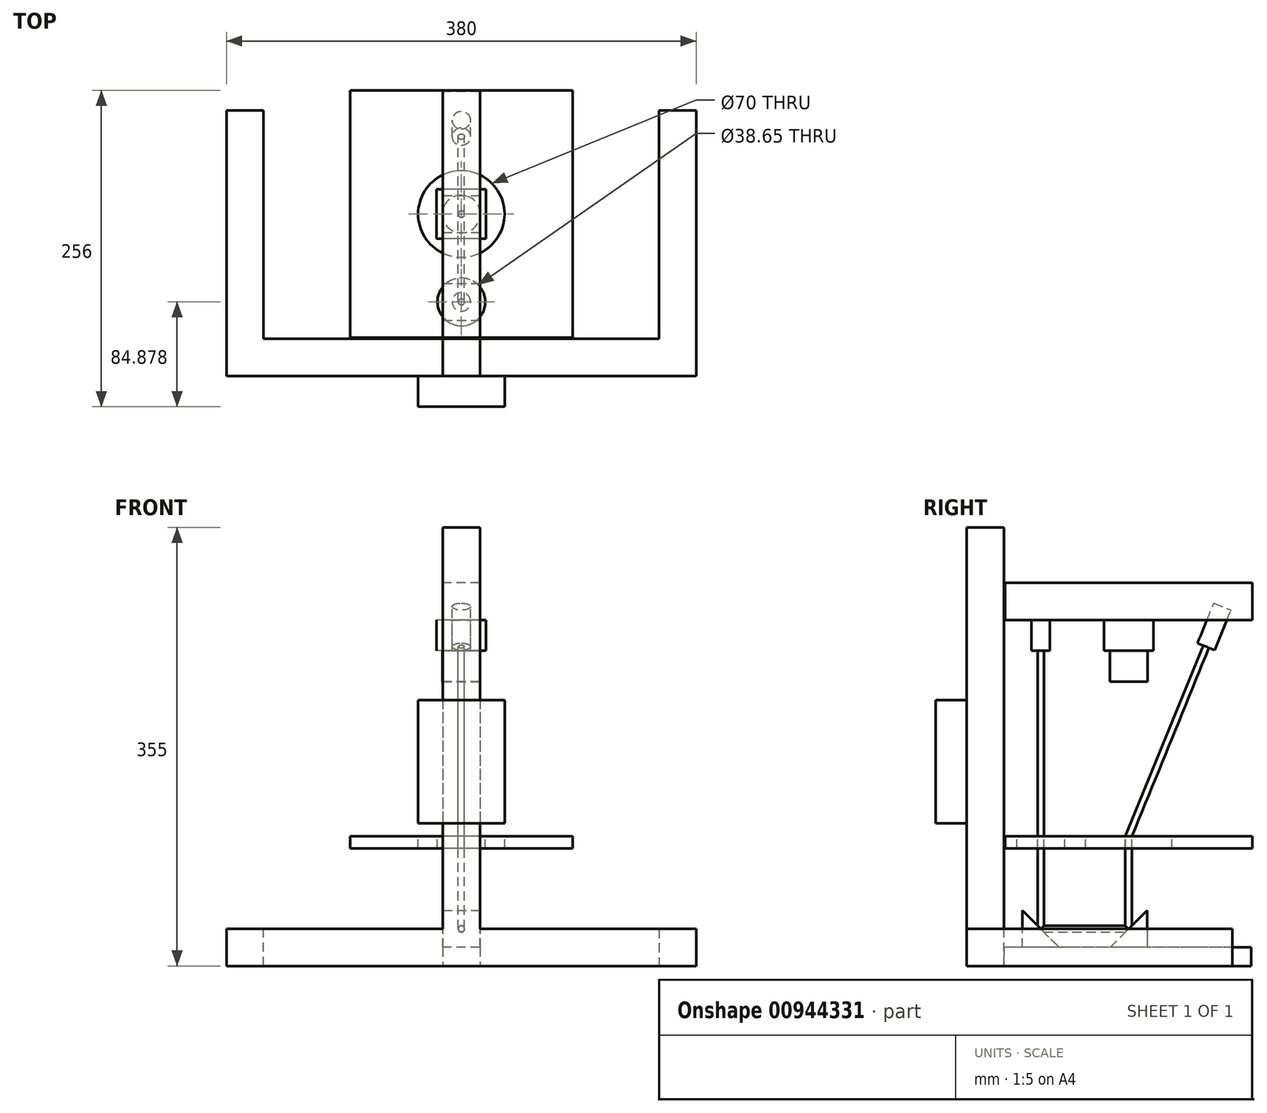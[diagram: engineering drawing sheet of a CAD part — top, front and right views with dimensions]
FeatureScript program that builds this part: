
annotation { "Feature Type Name" : "Feature", "Feature Type Description" : "" }
export const myFeature = defineFeature(function(context is Context, id is Id, definition is map)
    precondition{}
    {
        {
            assignVariable(context, id + "F0", {"name" : "Seccion", "anyValue" : 30});
        }
        {
            assignVariable(context, id + "F1", {"name" : "AxisX", "anyValue" : 200});
        }
        {
            assignVariable(context, id + "F2", {"name" : "AxisY", "anyValue" : 350});
        }
        {
            assignVariable(context, id + "F3", {"name" : "AxisZ", "anyValue" : 340});
        }
        {
            var Q0;
            Q0=qCreatedBy(makeId("Top.planeOp"),FACE);
            var sketch = newSketch(context, id + "F4", { "sketchPlane" : qUnion([Q0])});
            skLineSegment(sketch, "E0", {"start": v(-141.57, 101.23) * mm, "end": v(-141.57, -98.77) * mm});
            skLineSegment(sketch, "E1", {"start": v(-141.57, -98.77) * mm, "end": v(208.43, -98.77) * mm});
            skLineSegment(sketch, "E2", {"start": v(208.43, -98.77) * mm, "end": v(208.43, 101.23) * mm});
            skPoint(sketch, "E3", {"position": v(33.43, -98.77) * mm});
            skLineSegment(sketch, "E4.bottom", {"start": v(18.43, -83.77) * mm, "end": v(48.43, -83.77) * mm});
            skLineSegment(sketch, "E4.top", {"start": v(18.43, -113.77) * mm, "end": v(48.43, -113.77) * mm});
            skLineSegment(sketch, "E4.left", {"start": v(18.43, -83.77) * mm, "end": v(18.43, -113.77) * mm});
            skLineSegment(sketch, "E4.right", {"start": v(48.43, -83.77) * mm, "end": v(48.43, -113.77) * mm});
            skSolve(sketch);
        }
        {
            var Q0;
            {var subQ5=sQuery(id+"F4.wireOp",EDGE,"E4.bottom");Q0=makeQuery(id+"F4.imprint","IMPRINT",FACE,{"disambiguationData":[TD([[makeQuery(id+"F4.imprint","IMPRINT",EDGE,{"derivedFrom":subQ5}),-1.0]])]});}
            var Q1;
            {var subQ5=sQuery(id+"F4.wireOp",EDGE,"E4.top");Q1=makeQuery(id+"F4.imprint","IMPRINT",FACE,{"disambiguationData":[TD([[makeQuery(id+"F4.imprint","IMPRINT",EDGE,{"derivedFrom":subQ5}),1.0]])]});}
            extrude(context, id + "F5", {"entities" : qUnion([Q0, Q1]), "depth" : (getVariable(context, 'AxisZ')) * mm, "offsetDistance" : 25 * mm});
        }
        {
            var Q0;
            Q0=qCreatedBy(makeId("Front.planeOp"),FACE);
            var Q1;
            Q1=sQuery(id+"F4.wireOp",VERTEX,"E0.start");
            cPlane(context, id + "F6", {"entities" : qUnion([Q0, Q1]), "cplaneType" : CPlaneType.PLANE_POINT, "offset" : 25 * mm, "width" : 150 * mm, "height" : 150 * mm});
        }
        {
            var Q0;
            Q0=qCreatedBy(id+"F6.planeOp",FACE);
            var sketch = newSketch(context, id + "F7", { "sketchPlane" : qUnion([Q0])});
            skLineSegment(sketch, "E5.bottom", {"start": v(-126.57, 15) * mm, "end": v(-156.57, 15) * mm});
            skLineSegment(sketch, "E5.top", {"start": v(-126.57, -15) * mm, "end": v(-156.57, -15) * mm});
            skLineSegment(sketch, "E5.left", {"start": v(-126.57, 15) * mm, "end": v(-126.57, -15) * mm});
            skLineSegment(sketch, "E5.right", {"start": v(-156.57, 15) * mm, "end": v(-156.57, -15) * mm});
            skPoint(sketch, "E5.middle", {"position": v(-141.57, 0) * mm});
            skLineSegment(sketch, "E6.bottom", {"start": v(223.43, 15) * mm, "end": v(193.43, 15) * mm});
            skLineSegment(sketch, "E6.top", {"start": v(223.43, -15) * mm, "end": v(193.43, -15) * mm});
            skLineSegment(sketch, "E6.left", {"start": v(223.43, 15) * mm, "end": v(223.43, -15) * mm});
            skLineSegment(sketch, "E6.right", {"start": v(193.43, 15) * mm, "end": v(193.43, -15) * mm});
            skPoint(sketch, "E6.middle", {"position": v(208.43, 0) * mm});
            skSolve(sketch);
        }
        {
            var Q0;
            Q0=makeQuery(id+"F7.imprint","IMPRINT",FACE,{"disambiguationData":[TD([[makeQuery(id+"F7.imprint","IMPRINT",EDGE,{"derivedFrom":sQuery(id+"F7.wireOp",EDGE,"E6.bottom")}),1.0]])]});
            var Q1;
            Q1=makeQuery(id+"F7.imprint","IMPRINT",FACE,{"disambiguationData":[TD([[makeQuery(id+"F7.imprint","IMPRINT",EDGE,{"derivedFrom":sQuery(id+"F7.wireOp",EDGE,"E5.bottom")}),1.0]])]});
            extrude(context, id + "F8", {"entities" : qUnion([Q0, Q1]), "depth" : (getVariable(context, 'AxisX') + getVariable(context, 'Seccion') / 2) * mm, "offsetDistance" : 25 * mm});
        }
        {
            var Q0;
            Q0=makeQuery(id+"F8.opExtrude","SWEPT_FACE",FACE,{"disambiguationData":[OSD([sQuery(id+"F7.wireOp",EDGE,"E5.right")])]});
            var sketch = newSketch(context, id + "F9", { "sketchPlane" : qUnion([Q0])});
            skLineSegment(sketch, "E7.bottom", {"start": v(113.77, 15) * mm, "end": v(83.77, 15) * mm});
            skLineSegment(sketch, "E7.top", {"start": v(113.77, -15) * mm, "end": v(83.77, -15) * mm});
            skLineSegment(sketch, "E7.left", {"start": v(113.77, 15) * mm, "end": v(113.77, -15) * mm});
            skLineSegment(sketch, "E7.right", {"start": v(83.77, 15) * mm, "end": v(83.77, -15) * mm});
            skSolve(sketch);
        }
        {
            var Q0;
            {var subQ4=sQuery(id+"F12.wireOp",EDGE,"E8.top");Q0=makeQuery(id+"F12.imprint","IMPRINT",FACE,{"disambiguationData":[TD([[makeQuery(id+"F12.imprint","IMPRINT",EDGE,{"derivedFrom":subQ4}),-1.0]])]});}
            var Q1;
            Q1=makeQuery(id+"F5.opExtrude","SWEPT_FACE",FACE,{"disambiguationData":[OSD([sQuery(id+"F4.wireOp",EDGE,"E4.bottom")])]});
            cPlane(context, id + "F10", {"entities" : qUnion([Q0, Q1]), "cplaneType" : CPlaneType.OFFSET, "offset" : 1 * mm, "width" : 150 * mm, "height" : 150 * mm});
        }
        {
            var Q0;
            Q0=makeQuery(id+"F9.imprint","IMPRINT",FACE,{"disambiguationData":[TD([[makeQuery(id+"F9.imprint","IMPRINT",EDGE,{"derivedFrom":sQuery(id+"F9.wireOp",EDGE,"E7.bottom")}),1.0]])]});
            extrude(context, id + "F11", {"entities" : qUnion([Q0]), "operationType" : NewBodyOperationType.ADD, "oppositeDirection" : true, "depth" : (getVariable(context, 'AxisY')) * mm, "offsetDistance" : 25 * mm});
        }
        {
            var Q0;
            Q0=qCreatedBy(id+"F10.planeOp",FACE);
            var sketch = newSketch(context, id + "F12", { "sketchPlane" : qUnion([Q0])});
            skLineSegment(sketch, "E8.bottom", {"start": v(-48.43, 295) * mm, "end": v(-18.43, 295) * mm});
            skLineSegment(sketch, "E8.top", {"start": v(-48.43, 265) * mm, "end": v(-18.43, 265) * mm});
            skLineSegment(sketch, "E8.left", {"start": v(-48.43, 295) * mm, "end": v(-48.43, 265) * mm});
            skLineSegment(sketch, "E8.right", {"start": v(-18.43, 295) * mm, "end": v(-18.43, 265) * mm});
            skLineSegment(sketch, "E9", {"start": v(-33.43, 265) * mm, "end": v(-33.43, -15) * mm, "construction": true});
            skLineSegment(sketch, "E10.bottom", {"start": v(-123.43, 90) * mm, "end": v(56.57, 90) * mm});
            skLineSegment(sketch, "E10.top", {"start": v(-123.43, 80) * mm, "end": v(56.57, 80) * mm});
            skLineSegment(sketch, "E10.left", {"start": v(-123.43, 90) * mm, "end": v(-123.43, 80) * mm});
            skLineSegment(sketch, "E10.right", {"start": v(56.57, 90) * mm, "end": v(56.57, 80) * mm});
            skPoint(sketch, "E10.middle", {"position": v(-33.43, 85) * mm});
            skLineSegment(sketch, "E11", {"start": v(-123.43, 80) * mm, "end": v(-123.43, 0) * mm, "construction": true});
            skSolve(sketch);
        }
        {
            var Q0;
            Q0=makeQuery(id+"F12.imprint","IMPRINT",FACE,{"disambiguationData":[TD([[makeQuery(id+"F12.imprint","IMPRINT",EDGE,{"derivedFrom":sQuery(id+"F12.wireOp",EDGE,"E8.bottom")}),-1.0]])]});
            extrude(context, id + "F13", {"entities" : qUnion([Q0]), "operationType" : NewBodyOperationType.ADD, "depth" : (getVariable(context, 'AxisX')) * mm, "offsetDistance" : 25 * mm});
        }
        {
            var Q0;
            Q0=makeQuery(id+"F12.imprint","IMPRINT",FACE,{"disambiguationData":[TD([[makeQuery(id+"F12.imprint","IMPRINT",EDGE,{"derivedFrom":sQuery(id+"F12.wireOp",EDGE,"E10.bottom")}),-1.0]])]});
            extrude(context, id + "F14", {"entities" : qUnion([Q0]), "depth" : (getVariable(context, 'AxisX')) * mm, "offsetDistance" : 25 * mm});
        }
        {
            var Q0;
            Q0=makeQuery(id+"F14.opExtrude","SWEPT_FACE",FACE,{"disambiguationData":[OSD([sQuery(id+"F12.wireOp",EDGE,"E10.bottom")])]});
            var sketch = newSketch(context, id + "F15", { "sketchPlane" : qUnion([Q0])});
            skCircle(sketch, "E12", {"center": v(33.43, 17.23) * mm, "radius": 35 * mm});
            skPoint(sketch, "E12.centerSnap0", {"position": v(123.43, 17.23) * mm});
            skPoint(sketch, "E12.centerSnap1", {"position": v(33.43, -82.77) * mm});
            skLineSegment(sketch, "E13", {"start": v(33.43, -82.77) * mm, "end": v(33.43, 17.23) * mm, "construction": true});
            skCircle(sketch, "E14", {"center": v(33.43, -53.9) * mm, "radius": 19.32 * mm});
            skCircle(sketch, "E15", {"center": v(33.43, 17.23) * mm, "radius": 2.5 * mm});
            skSolve(sketch);
        }
        {
            var Q0;
            Q0=makeQuery(id+"F15.imprint","IMPRINT",FACE,{"disambiguationData":[TD([[makeQuery(id+"F15.imprint","IMPRINT",EDGE,{"derivedFrom":sQuery(id+"F15.wireOp",EDGE,"E14")}),1.0]])]});
            var Q1;
            Q1=makeQuery(id+"F15.imprint","IMPRINT",FACE,{"disambiguationData":[TD([[makeQuery(id+"F15.imprint","IMPRINT",EDGE,{"derivedFrom":sQuery(id+"F15.wireOp",EDGE,"E12")}),1.0]])]});
            var Q2;
            Q2=makeQuery(id+"F15.imprint","IMPRINT",FACE,{"disambiguationData":[TD([[makeQuery(id+"F15.imprint","IMPRINT",EDGE,{"derivedFrom":sQuery(id+"F15.wireOp",EDGE,"E15")}),1.0]])]});
            extrude(context, id + "F16", {"entities" : qUnion([Q0, Q1, Q2]), "operationType" : NewBodyOperationType.REMOVE, "oppositeDirection" : true, "depth" : 10 * mm, "offsetDistance" : 25 * mm});
        }
        {
            var Q0;
            Q0=makeQuery(id+"F13.opExtrude","SWEPT_FACE",FACE,{"disambiguationData":[OSD([sQuery(id+"F12.wireOp",EDGE,"E8.top")])]});
            var sketch = newSketch(context, id + "F17", { "sketchPlane" : qUnion([Q0])});
            skPoint(sketch, "E16.middle", {"position": v(33.43, -17.23) * mm});
            skPoint(sketch, "E16.middle.positionSnap0", {"position": v(48.43, -17.23) * mm});
            skPoint(sketch, "E16.centerSnap0", {"position": v(48.43, -17.23) * mm});
            skLineSegment(sketch, "E17.bottom", {"start": v(53.43, 2.77) * mm, "end": v(13.43, 2.77) * mm});
            skLineSegment(sketch, "E17.top", {"start": v(53.43, -37.23) * mm, "end": v(13.43, -37.23) * mm});
            skLineSegment(sketch, "E17.left", {"start": v(53.43, 2.77) * mm, "end": v(53.43, -37.23) * mm});
            skLineSegment(sketch, "E17.right", {"start": v(13.43, 2.77) * mm, "end": v(13.43, -37.23) * mm});
            skSolve(sketch);
        }
        {
            var Q0;
            {var subQ0=sQuery(id+"F17.wireOp",EDGE,"E17.bottom");var subQ1=sQuery(id+"F12.wireOp",EDGE,"E8.top");var subQ2=makeQuery(id+"F13.opExtrude","SWEPT_EDGE",EDGE,{"disambiguationData":[OSD([subQ1,sQuery(id+"F12.wireOp",EDGE,"E8.left")])]});var subQ3=makeQuery(id+"F17.imprint","INTERSECT",VERTEX,{"derivedFrom":[subQ2,subQ0]});Q0=makeQuery(id+"F17.imprint","IMPRINT",FACE,{"disambiguationData":[TD([[makeQuery(id+"F17.imprint","IMPRINT",EDGE,{"disambiguationData":[TD([[subQ3,-1.0]])],"derivedFrom":subQ0}),1.0]])]});}
            var Q1;
            {var subQ4=sQuery(id+"F17.wireOp",EDGE,"E17.right");Q1=makeQuery(id+"F17.imprint","IMPRINT",FACE,{"disambiguationData":[TD([[makeQuery(id+"F17.imprint","IMPRINT",EDGE,{"derivedFrom":subQ4}),1.0]])]});}
            var Q2;
            {var subQ4=sQuery(id+"F17.wireOp",EDGE,"E17.left");Q2=makeQuery(id+"F17.imprint","IMPRINT",FACE,{"disambiguationData":[TD([[makeQuery(id+"F17.imprint","IMPRINT",EDGE,{"derivedFrom":subQ4}),-1.0]])]});}
            var Q3;
            {var subQ0=sQuery(id+"F17.wireOp",EDGE,"qo7p0JnK-KsdK-9qBr-5w5p-VYG7PEEHzOIh");var subQ1=sQuery(id+"F12.wireOp",EDGE,"E8.top");var subQ2=makeQuery(id+"F13.opExtrude","SWEPT_EDGE",EDGE,{"disambiguationData":[OSD([subQ1,sQuery(id+"F12.wireOp",EDGE,"E8.right")])]});var subQ3=makeQuery(id+"F17.imprint","INTERSECT",VERTEX,{"disambiguationData":[OD(0.0)],"derivedFrom":[subQ2,subQ0]});Q3=makeQuery(id+"F17.imprint","IMPRINT",FACE,{"disambiguationData":[TD([[makeQuery(id+"F17.imprint","IMPRINT",EDGE,{"disambiguationData":[TD([[subQ3,1.0]])],"derivedFrom":subQ0}),1.0]])]});}
            var Q4;
            {var subQ0=sQuery(id+"F17.wireOp",EDGE,"E17.top");var subQ1=sQuery(id+"F12.wireOp",EDGE,"E8.top");var subQ2=makeQuery(id+"F13.opExtrude","SWEPT_EDGE",EDGE,{"disambiguationData":[OSD([subQ1,sQuery(id+"F12.wireOp",EDGE,"E8.left")])]});var subQ3=makeQuery(id+"F17.imprint","INTERSECT",VERTEX,{"derivedFrom":[subQ2,subQ0]});Q4=makeQuery(id+"F17.imprint","IMPRINT",FACE,{"disambiguationData":[TD([[makeQuery(id+"F17.imprint","IMPRINT",EDGE,{"disambiguationData":[TD([[subQ3,-1.0]])],"derivedFrom":subQ0}),-1.0]])]});}
            var Q5;
            {var subQ0=sQuery(id+"F17.wireOp",EDGE,"qo7p0JnK-KsdK-9qBr-5w5p-VYG7PEEHzOIh");var subQ1=makeQuery(id+"F13.opExtrude","SWEPT_EDGE",EDGE,{"disambiguationData":[OSD([sQuery(id+"F12.wireOp",EDGE,"E8.top"),sQuery(id+"F12.wireOp",EDGE,"E8.right")])]});var subQ2=makeQuery(id+"F17.imprint","INTERSECT",VERTEX,{"disambiguationData":[OD(0.0)],"derivedFrom":[subQ1,subQ0]});Q5=makeQuery(id+"F17.imprint","IMPRINT",FACE,{"disambiguationData":[TD([[makeQuery(id+"F17.imprint","IMPRINT",EDGE,{"disambiguationData":[TD([[subQ2,-1.0]])],"derivedFrom":subQ0}),1.0]])]});}
            var Q6;
            {var subQ0=sQuery(id+"F17.wireOp",EDGE,"qo7p0JnK-KsdK-9qBr-5w5p-VYG7PEEHzOIh");var subQ1=makeQuery(id+"F13.opExtrude","SWEPT_EDGE",EDGE,{"disambiguationData":[OSD([sQuery(id+"F12.wireOp",EDGE,"E8.top"),sQuery(id+"F12.wireOp",EDGE,"E8.left")])]});var subQ2=makeQuery(id+"F17.imprint","INTERSECT",VERTEX,{"disambiguationData":[OD(0.0)],"derivedFrom":[subQ1,subQ0]});Q6=makeQuery(id+"F17.imprint","IMPRINT",FACE,{"disambiguationData":[TD([[makeQuery(id+"F17.imprint","IMPRINT",EDGE,{"disambiguationData":[TD([[subQ2,1.0]])],"derivedFrom":subQ0}),1.0]])]});}
            extrude(context, id + "F18", {"entities" : qUnion([Q0, Q1, Q2, Q3, Q4, Q5, Q6]), "depth" : 25 * mm, "offsetDistance" : 25 * mm});
        }
        {
            var Q0;
            Q0=makeQuery(id+"F18.opExtrude","CAP_FACE",FACE,{"disambiguationData":[OSD([sQuery(id+"F17.wireOp",EDGE,"E17.bottom"),sQuery(id+"F17.wireOp",EDGE,"E17.top"),sQuery(id+"F17.wireOp",EDGE,"E17.left"),sQuery(id+"F17.wireOp",EDGE,"E17.right")])],"isStart":false});
            var sketch = newSketch(context, id + "F19", { "sketchPlane" : qUnion([Q0])});
            skCircle(sketch, "E18", {"center": v(33.43, -17.23) * mm, "radius": 15.27 * mm});
            skSolve(sketch);
        }
        {
            var Q0;
            Q0=makeQuery(id+"F19.imprint","IMPRINT",FACE,{"disambiguationData":[TD([[makeQuery(id+"F19.imprint","IMPRINT",EDGE,{"derivedFrom":sQuery(id+"F19.wireOp",EDGE,"E18")}),1.0]])]});
            var Q1;
            Q1=sQuery(id+"F17.wireOp",EDGE,"qo7p0JnK-KsdK-9qBr-5w5p-VYG7PEEHzOIh");
            extrude(context, id + "F20", {"entities" : qUnion([Q0]), "surfaceEntities" : qUnion([Q1]), "depth" : 25 * mm, "offsetDistance" : 25 * mm});
        }
        {
            var Q0;
            Q0=sQuery(id+"F15.wireOp",EDGE,"E13");
            cPlane(context, id + "F21", {"entities" : qUnion([Q0]), "cplaneType" : CPlaneType.LINE_ANGLE, "offset" : 25 * mm, "angle" : 90 * degree, "width" : 150 * mm, "height" : 150 * mm});
        }
        {
            var Q0;
            Q0=qCreatedBy(id+"F21.planeOp",FACE);
            var sketch = newSketch(context, id + "F22", { "sketchPlane" : qUnion([Q0])});
            skLineSegment(sketch, "E19", {"start": v(17.23, 90) * mm, "end": v(93.1, 275.8) * mm, "construction": true});
            skSolve(sketch);
        }
        {
            var Q0;
            Q0=sQuery(id+"F22.wireOp",EDGE,"E19");
            var Q1;
            Q1=sQuery(id+"F22.wireOp",VERTEX,"E19.end");
            cPlane(context, id + "F23", {"entities" : qUnion([Q0, Q1]), "cplaneType" : CPlaneType.LINE_POINT, "offset" : 25 * mm, "width" : 150 * mm, "height" : 150 * mm});
        }
        {
            var Q0;
            Q0=qCreatedBy(id+"F23.planeOp",FACE);
            var sketch = newSketch(context, id + "F24", { "sketchPlane" : qUnion([Q0])});
            skCircle(sketch, "E20", {"center": v(33.43, -18.07) * mm, "radius": 7.5 * mm});
            skSolve(sketch);
        }
        {
            var Q0;
            Q0=makeQuery(id+"F24.imprint","IMPRINT",FACE,{"disambiguationData":[TD([[makeQuery(id+"F24.imprint","IMPRINT",EDGE,{"derivedFrom":sQuery(id+"F24.wireOp",EDGE,"E20")}),1.0]])]});
            extrude(context, id + "F25", {"entities" : qUnion([Q0]), "oppositeDirection" : true, "depth" : 35 * mm, "offsetDistance" : 25 * mm});
        }
        {
            var Q0;
            Q0=makeQuery(id+"F11.boolean.opBoolean","MERGE",FACE,{"derivedFrom":[makeQuery(id+"F5.opExtrude","SWEPT_FACE",FACE,{"disambiguationData":[OSD([sQuery(id+"F4.wireOp",EDGE,"E4.top")])]}),makeQuery(id+"F8.opExtrude","CAP_FACE",FACE,{"disambiguationData":[OSD([sQuery(id+"F7.wireOp",EDGE,"E5.bottom"),sQuery(id+"F7.wireOp",EDGE,"E5.top"),sQuery(id+"F7.wireOp",EDGE,"E5.left"),sQuery(id+"F7.wireOp",EDGE,"E5.right")])],"isStart":false}),makeQuery(id+"F8.opExtrude","CAP_FACE",FACE,{"disambiguationData":[OSD([sQuery(id+"F7.wireOp",EDGE,"E6.bottom"),sQuery(id+"F7.wireOp",EDGE,"E6.top"),sQuery(id+"F7.wireOp",EDGE,"E6.left"),sQuery(id+"F7.wireOp",EDGE,"E6.right")])],"isStart":false}),makeQuery(id+"F11.opExtrude","SWEPT_FACE",FACE,{"disambiguationData":[OSD([sQuery(id+"F9.wireOp",EDGE,"E7.left")])]})]});
            var sketch = newSketch(context, id + "F26", { "sketchPlane" : qUnion([Q0])});
            skLineSegment(sketch, "E21.bottom", {"start": v(68.43, 200.3) * mm, "end": v(-1.57, 200.3) * mm});
            skLineSegment(sketch, "E21.top", {"start": v(68.43, 100.3) * mm, "end": v(-1.57, 100.3) * mm});
            skLineSegment(sketch, "E21.left", {"start": v(68.43, 200.3) * mm, "end": v(68.43, 100.3) * mm});
            skLineSegment(sketch, "E21.right", {"start": v(-1.57, 200.3) * mm, "end": v(-1.57, 100.3) * mm});
            skPoint(sketch, "E21.middle", {"position": v(33.43, 150.3) * mm});
            skSolve(sketch);
        }
        {
            var Q0;
            {var subQ0=sQuery(id+"F26.wireOp",EDGE,"E21.left");Q0=makeQuery(id+"F26.imprint","IMPRINT",FACE,{"disambiguationData":[TD([[makeQuery(id+"F26.imprint","IMPRINT",EDGE,{"derivedFrom":subQ0}),-1.0]])]});}
            var Q1;
            {var subQ0=sQuery(id+"F26.wireOp",EDGE,"E21.bottom");var subQ1=sQuery(id+"F4.wireOp",EDGE,"E4.top");var subQ2=makeQuery(id+"F5.opExtrude","SWEPT_EDGE",EDGE,{"disambiguationData":[OSD([subQ1,sQuery(id+"F4.wireOp",EDGE,"E4.right")])]});var subQ3=makeQuery(id+"F26.imprint","INTERSECT",VERTEX,{"derivedFrom":[subQ2,subQ0]});Q1=makeQuery(id+"F26.imprint","IMPRINT",FACE,{"disambiguationData":[TD([[makeQuery(id+"F26.imprint","IMPRINT",EDGE,{"disambiguationData":[TD([[subQ3,-1.0]])],"derivedFrom":subQ0}),1.0]])]});}
            var Q2;
            {var subQ0=sQuery(id+"F26.wireOp",EDGE,"E21.right");Q2=makeQuery(id+"F26.imprint","IMPRINT",FACE,{"disambiguationData":[TD([[makeQuery(id+"F26.imprint","IMPRINT",EDGE,{"derivedFrom":subQ0}),1.0]])]});}
            extrude(context, id + "F27", {"entities" : qUnion([Q0, Q1, Q2]), "depth" : 25 * mm, "offsetDistance" : 25 * mm});
        }
        {
            var Q0;
            {var subQ1=sQuery(id+"F12.wireOp",EDGE,"E8.top");var subQ6=makeQuery(id+"F13.opExtrude","CAP_EDGE",EDGE,{"disambiguationData":[OSD([subQ1])],"isStart":true});Q0=makeQuery(id+"F17.imprint","IMPRINT",FACE,{"disambiguationData":[TD([[makeQuery(id+"F17.imprint","IMPRINT",EDGE,{"derivedFrom":subQ6}),1.0]])]});}
            var sketch = newSketch(context, id + "F28", { "sketchPlane" : qUnion([Q0])});
            skCircle(sketch, "E22", {"center": v(33.43, 53.9) * mm, "radius": 7.5 * mm});
            skSolve(sketch);
        }
        {
            var Q0;
            Q0 = qSketchRegion(id + "F28", true);
            extrude(context, id + "F29", {"entities" : qUnion([Q0]), "depth" : 25 * mm, "offsetDistance" : 25 * mm});
        }
        {
            var Q0;
            Q0=makeQuery(id+"F11.boolean.opBoolean","MERGE",FACE,{"derivedFrom":[makeQuery(id+"F5.opExtrude","SWEPT_FACE",FACE,{"disambiguationData":[OSD([sQuery(id+"F4.wireOp",EDGE,"E4.bottom")])]}),makeQuery(id+"F11.opExtrude","SWEPT_FACE",FACE,{"disambiguationData":[OSD([sQuery(id+"F9.wireOp",EDGE,"E7.right")])]})]});
            var sketch = newSketch(context, id + "F30", { "sketchPlane" : qUnion([Q0])});
            skLineSegment(sketch, "E23.bottom", {"start": v(-48.43, 0) * mm, "end": v(-18.43, 0) * mm});
            skLineSegment(sketch, "E23.top", {"start": v(-48.43, -15) * mm, "end": v(-18.43, -15) * mm});
            skLineSegment(sketch, "E23.left", {"start": v(-48.43, 0) * mm, "end": v(-48.43, -15) * mm});
            skLineSegment(sketch, "E23.right", {"start": v(-18.43, 0) * mm, "end": v(-18.43, -15) * mm});
            skSolve(sketch);
        }
        {
            var Q0;
            Q0 = qSketchRegion(id + "F30", true);
            extrude(context, id + "F31", {"entities" : qUnion([Q0]), "operationType" : NewBodyOperationType.ADD, "depth" : (getVariable(context, 'AxisX')) * mm, "offsetDistance" : 25 * mm});
        }
        {
            var Q0;
            Q0=makeQuery(id+"F31.opExtrude","SWEPT_FACE",FACE,{"disambiguationData":[OSD([sQuery(id+"F30.wireOp",EDGE,"E23.bottom")])]});
            var sketch = newSketch(context, id + "F32", { "sketchPlane" : qUnion([Q0])});
            skPoint(sketch, "E24", {"position": v(33.43, -53.9) * mm});
            skPoint(sketch, "E25", {"position": v(33.43, 17.23) * mm});
            skLineSegment(sketch, "E26.bottom", {"start": v(18.43, -68.9) * mm, "end": v(48.43, -68.9) * mm});
            skLineSegment(sketch, "E26.top", {"start": v(18.43, -38.9) * mm, "end": v(48.43, -38.9) * mm});
            skLineSegment(sketch, "E26.left", {"start": v(18.43, -68.9) * mm, "end": v(18.43, -38.9) * mm});
            skLineSegment(sketch, "E26.right", {"start": v(48.43, -68.9) * mm, "end": v(48.43, -38.9) * mm});
            skLineSegment(sketch, "E27.bottom", {"start": v(48.43, 32.23) * mm, "end": v(18.43, 32.23) * mm});
            skLineSegment(sketch, "E27.top", {"start": v(48.43, 2.23) * mm, "end": v(18.43, 2.23) * mm});
            skLineSegment(sketch, "E27.left", {"start": v(48.43, 32.23) * mm, "end": v(48.43, 2.23) * mm});
            skLineSegment(sketch, "E27.right", {"start": v(18.43, 32.23) * mm, "end": v(18.43, 2.23) * mm});
            skSolve(sketch);
        }
        {
            var Q0;
            Q0=makeQuery(id+"F31.opExtrude","SWEPT_FACE",FACE,{"disambiguationData":[OSD([sQuery(id+"F30.wireOp",EDGE,"E23.left")])]});
            var sketch = newSketch(context, id + "F33", { "sketchPlane" : qUnion([Q0])});
            skLineSegment(sketch, "E28", {"start": v(-68.9, 0) * mm, "end": v(-68.9, 30) * mm});
            skLineSegment(sketch, "E29", {"start": v(-68.9, 30) * mm, "end": v(-38.9, 0) * mm});
            skLineSegment(sketch, "E30", {"start": v(2.23, 0) * mm, "end": v(32.23, 30) * mm});
            skLineSegment(sketch, "E31", {"start": v(32.23, 30) * mm, "end": v(32.23, 0) * mm});
            skSolve(sketch);
        }
        {
            var Q0;
            {var subQ0=sQuery(id+"F33.wireOp",EDGE,"E28");Q0=makeQuery(id+"F33.imprint","IMPRINT",FACE,{"disambiguationData":[TD([[makeQuery(id+"F33.imprint","IMPRINT",EDGE,{"derivedFrom":subQ0}),-1.0]])]});}
            var Q1;
            {var subQ0=sQuery(id+"F33.wireOp",EDGE,"E30");Q1=makeQuery(id+"F33.imprint","IMPRINT",FACE,{"disambiguationData":[TD([[makeQuery(id+"F33.imprint","IMPRINT",EDGE,{"derivedFrom":subQ0}),-1.0]])]});}
            extrude(context, id + "F34", {"entities" : qUnion([Q0, Q1]), "oppositeDirection" : true, "depth" : (getVariable(context, 'Seccion')) * mm, "offsetDistance" : 25 * mm});
        }
        {
            var Q0;
            Q0=makeQuery(id+"F34.opExtrude","SWEPT_FACE",FACE,{"disambiguationData":[OSD([sQuery(id+"F33.wireOp",EDGE,"E30")])]});
            var sketch = newSketch(context, id + "F35", { "sketchPlane" : qUnion([Q0])});
            skPoint(sketch, "E32", {"position": v(33.43, 22.8) * mm});
            skPoint(sketch, "E32.positionSnap0", {"position": v(33.43, 44) * mm});
            skPoint(sketch, "E32.positionSnap1", {"position": v(48.43, 22.8) * mm});
            skCircle(sketch, "E33", {"center": v(33.43, 22.8) * mm, "radius": 2.5 * mm});
            skSolve(sketch);
        }
        {
            var Q0;
            Q0=makeQuery(id+"F34.opExtrude","SWEPT_FACE",FACE,{"disambiguationData":[OSD([sQuery(id+"F33.wireOp",EDGE,"E29")])]});
            var sketch = newSketch(context, id + "F36", { "sketchPlane" : qUnion([Q0])});
            skPoint(sketch, "E34", {"position": v(-33.43, 48.71) * mm});
            skPoint(sketch, "E34.positionSnap0", {"position": v(-33.43, 69.93) * mm});
            skPoint(sketch, "E34.positionSnap1", {"position": v(-48.43, 48.71) * mm});
            skCircle(sketch, "E35", {"center": v(-33.43, 48.71) * mm, "radius": 2.5 * mm});
            skSolve(sketch);
        }
        {
            var Q0;
            Q0=sQuery(id+"F36.wireOp",VERTEX,"E34");
            var Q1;
            Q1=sQuery(id+"F35.wireOp",VERTEX,"E32");
            var Q2;
            Q2=sQuery(id+"F15.wireOp",VERTEX,"E14.center");
            cPlane(context, id + "F37", {"entities" : qUnion([Q0, Q1, Q2]), "cplaneType" : CPlaneType.THREE_POINT, "offset" : 25 * mm, "width" : 150 * mm, "height" : 150 * mm});
        }
        {
            var Q0;
            Q0=makeQuery(id+"F29.opExtrude","CAP_FACE",FACE,{"disambiguationData":[OSD([sQuery(id+"F28.wireOp",EDGE,"E22")])],"isStart":false});
            var sketch = newSketch(context, id + "F38", { "sketchPlane" : qUnion([Q0])});
            skCircle(sketch, "E36", {"center": v(33.43, 53.9) * mm, "radius": 2.5 * mm});
            skSolve(sketch);
        }
        {
            var Q0;
            Q0=makeQuery(id+"F25.opExtrude","CAP_FACE",FACE,{"disambiguationData":[OSD([sQuery(id+"F24.wireOp",EDGE,"E20")])],"isStart":false});
            var sketch = newSketch(context, id + "F39", { "sketchPlane" : qUnion([Q0])});
            skCircle(sketch, "E37", {"center": v(33.43, 18.07) * mm, "radius": 2.5 * mm});
            skSolve(sketch);
        }
        {
            var Q0;
            Q0=makeQuery(id+"F39.imprint","IMPRINT",FACE,{"disambiguationData":[TD([[makeQuery(id+"F39.imprint","IMPRINT",EDGE,{"derivedFrom":sQuery(id+"F39.wireOp",EDGE,"E37")}),1.0]])]});
            var Q1;
            Q1=makeQuery(id+"F14.opExtrude","SWEPT_FACE",FACE,{"disambiguationData":[OSD([sQuery(id+"F12.wireOp",EDGE,"E10.bottom")])]});
            extrude(context, id + "F40", {"entities" : qUnion([Q0]), "endBound" : BoundingType.UP_TO_SURFACE, "depth" : 25 * mm, "endBoundEntityFace" : qUnion([Q1]), "offsetDistance" : 25 * mm});
        }
        {
            var Q0;
            Q0=makeQuery(id+"F38.imprint","IMPRINT",FACE,{"disambiguationData":[TD([[makeQuery(id+"F38.imprint","IMPRINT",EDGE,{"derivedFrom":sQuery(id+"F38.wireOp",EDGE,"E36")}),1.0]])]});
            extrude(context, id + "F41", {"entities" : qUnion([Q0]), "endBound" : BoundingType.UP_TO_NEXT, "depth" : 25 * mm, "offsetDistance" : 25 * mm});
        }
        {
            var Q0;
            Q0=makeQuery(id+"F40.opExtrude","CAP_FACE",FACE,{"disambiguationData":[OSD([sQuery(id+"F39.wireOp",EDGE,"E37")])],"isStart":false});
            extrude(context, id + "F42", {"entities" : qUnion([Q0]), "endBound" : BoundingType.UP_TO_NEXT, "depth" : 25 * mm, "offsetDistance" : 25 * mm});
        }
        {
            var Q0;
            Q0=makeQuery(id+"F34.opExtrude","SWEPT_FACE",FACE,{"disambiguationData":[OSD([sQuery(id+"F33.wireOp",EDGE,"E31")])]});
            var sketch = newSketch(context, id + "F43", { "sketchPlane" : qUnion([Q0])});
            skCircle(sketch, "E38", {"center": v(-33.43, 15) * mm, "radius": 2.5 * mm});
            skSolve(sketch);
        }
        {
            var Q0;
            Q0=makeQuery(id+"F43.imprint","IMPRINT",FACE,{"disambiguationData":[TD([[makeQuery(id+"F43.imprint","IMPRINT",EDGE,{"derivedFrom":sQuery(id+"F43.wireOp",EDGE,"E38")}),1.0]])]});
            var Q1;
            Q1=makeQuery(id+"F34.opExtrude","SWEPT_FACE",FACE,{"disambiguationData":[OSD([sQuery(id+"F33.wireOp",EDGE,"E29")])]});
            extrude(context, id + "F44", {"entities" : qUnion([Q0]), "operationType" : NewBodyOperationType.ADD, "endBound" : BoundingType.UP_TO_SURFACE, "oppositeDirection" : true, "depth" : 25 * mm, "endBoundEntityFace" : qUnion([Q1]), "offsetDistance" : 25 * mm});
        }
        {
            var Q0;
            Q0=makeQuery(id+"F15.imprint","IMPRINT",FACE,{"disambiguationData":[TD([[makeQuery(id+"F15.imprint","IMPRINT",EDGE,{"derivedFrom":sQuery(id+"F15.wireOp",EDGE,"E12")}),1.0]])]});
            var Q1;
            Q1=makeQuery(id+"F15.imprint","IMPRINT",FACE,{"disambiguationData":[TD([[makeQuery(id+"F15.imprint","IMPRINT",EDGE,{"derivedFrom":sQuery(id+"F15.wireOp",EDGE,"E14")}),1.0]])]});
            extrude(context, id + "F45", {"entities" : qUnion([Q0, Q1]), "oppositeDirection" : true, "depth" : 10 * mm, "offsetDistance" : 25 * mm});
        }
    });
